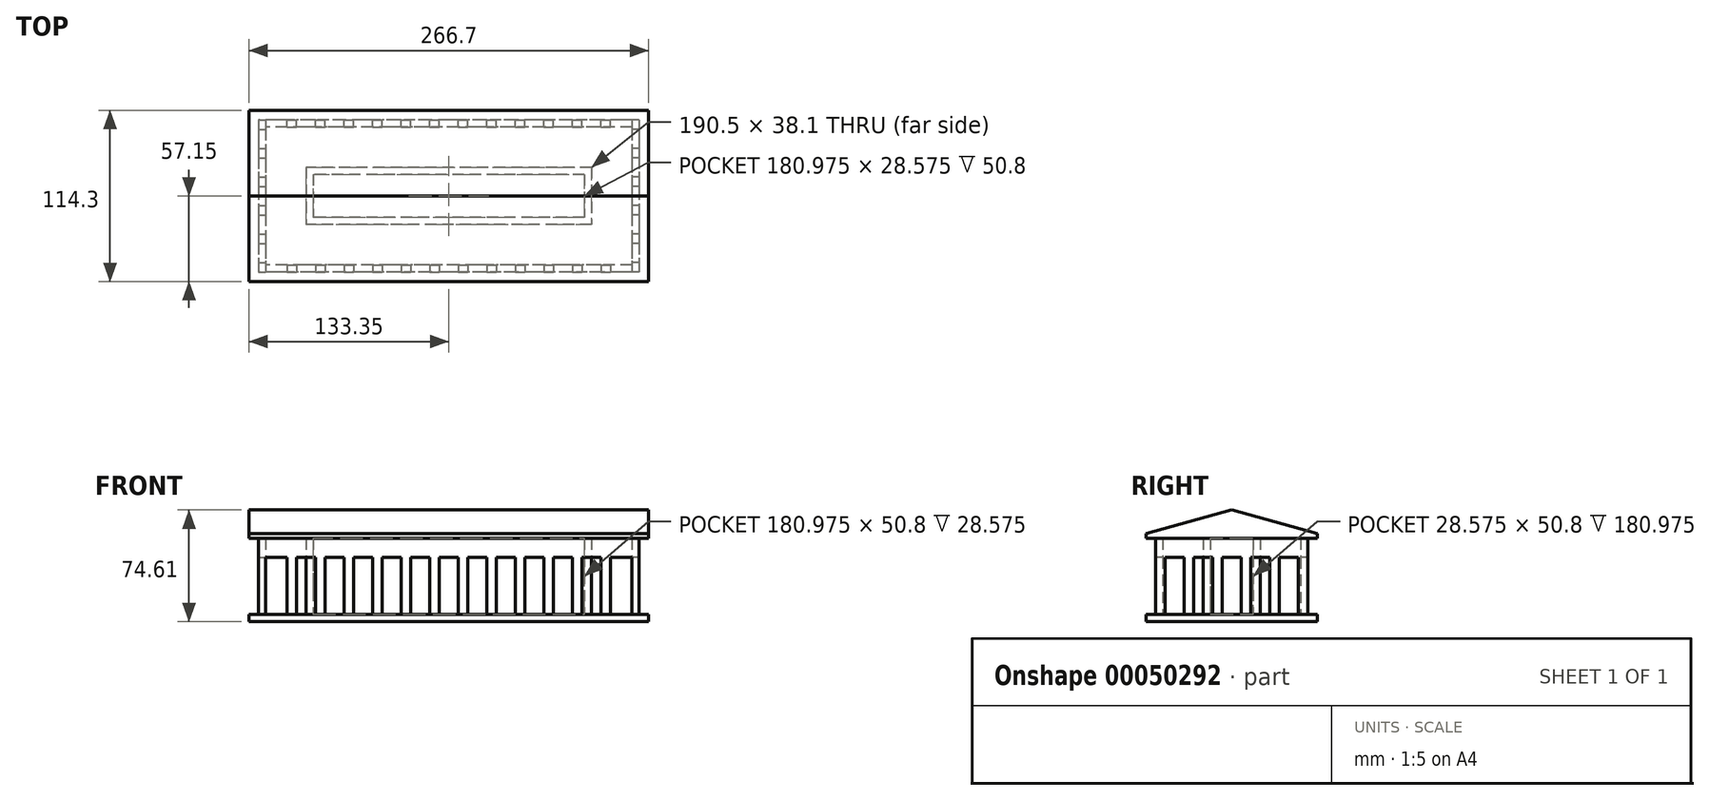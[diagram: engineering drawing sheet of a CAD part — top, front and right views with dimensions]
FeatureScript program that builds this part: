
annotation { "Feature Type Name" : "Feature", "Feature Type Description" : "" }
export const myFeature = defineFeature(function(context is Context, id is Id, definition is map)
    precondition{}
    {
        {
            var Q0;
            Q0=qCreatedBy(makeId("Top.planeOp"),FACE);
            var sketch = newSketch(context, id + "F0", { "sketchPlane" : qUnion([Q0])});
            skLineSegment(sketch, "E0.bottom", {"start": v(0, 0) * mm, "end": v(-266.7, 0) * mm});
            skLineSegment(sketch, "E0.top", {"start": v(0, -114.3) * mm, "end": v(-266.7, -114.3) * mm});
            skLineSegment(sketch, "E0.left", {"start": v(0, 0) * mm, "end": v(0, -114.3) * mm});
            skLineSegment(sketch, "E0.right", {"start": v(-266.7, 0) * mm, "end": v(-266.7, -114.3) * mm});
            skSolve(sketch);
        }
        {
            var Q0;
            Q0=qSketchRegion(id+"F0",true);
            var Q1;
            Q1=qSketchRegion(id+"FEWzJ1hWetXT4Pq_1",true);
            extrude(context, id + "F1", {"entities" : qUnion([Q0, Q1]), "depth" : 4.78 * mm});
        }
        {
            var Q0;
            Q0=makeQuery(id+"F1.opExtrude","CAP_FACE",FACE,{"disambiguationData":[OSD([sQuery(id+"F0.wireOp",EDGE,"E0.bottom"),sQuery(id+"F0.wireOp",EDGE,"E0.top"),sQuery(id+"F0.wireOp",EDGE,"E0.left"),sQuery(id+"F0.wireOp",EDGE,"E0.right")])],"isStart":false});
            var sketch = newSketch(context, id + "F2", { "sketchPlane" : qUnion([Q0])});
            skLineSegment(sketch, "E1.bottom", {"start": v(-260.35, -101.6) * mm, "end": v(-255.59, -101.6) * mm});
            skLineSegment(sketch, "E1.top", {"start": v(-260.35, -107.95) * mm, "end": v(-255.59, -107.95) * mm});
            skLineSegment(sketch, "E1.left", {"start": v(-260.35, -101.6) * mm, "end": v(-260.35, -107.95) * mm});
            skLineSegment(sketch, "E1.right", {"start": v(-255.59, -101.6) * mm, "end": v(-255.59, -107.95) * mm});
            skLineSegment(sketch, "E2.0.1.0", {"start": v(-260.35, -88.9) * mm, "end": v(-255.59, -88.9) * mm});
            skLineSegment(sketch, "E2.0.1.1", {"start": v(-255.59, -82.55) * mm, "end": v(-255.59, -88.9) * mm});
            skLineSegment(sketch, "E2.0.1.2", {"start": v(-260.35, -82.55) * mm, "end": v(-260.35, -88.9) * mm});
            skLineSegment(sketch, "E2.0.1.3", {"start": v(-260.35, -82.55) * mm, "end": v(-255.59, -82.55) * mm});
            skLineSegment(sketch, "E2.0.2.0", {"start": v(-260.35, -69.85) * mm, "end": v(-255.59, -69.85) * mm});
            skLineSegment(sketch, "E2.0.2.1", {"start": v(-255.59, -63.5) * mm, "end": v(-255.59, -69.85) * mm});
            skLineSegment(sketch, "E2.0.2.2", {"start": v(-260.35, -63.5) * mm, "end": v(-260.35, -69.85) * mm});
            skLineSegment(sketch, "E2.0.2.3", {"start": v(-260.35, -63.5) * mm, "end": v(-255.59, -63.5) * mm});
            skLineSegment(sketch, "E2.0.3.0", {"start": v(-260.35, -50.8) * mm, "end": v(-255.59, -50.8) * mm});
            skLineSegment(sketch, "E2.0.3.1", {"start": v(-255.59, -44.45) * mm, "end": v(-255.59, -50.8) * mm});
            skLineSegment(sketch, "E2.0.3.2", {"start": v(-260.35, -44.45) * mm, "end": v(-260.35, -50.8) * mm});
            skLineSegment(sketch, "E2.0.3.3", {"start": v(-260.35, -44.45) * mm, "end": v(-255.59, -44.45) * mm});
            skLineSegment(sketch, "E2.0.4.0", {"start": v(-260.35, -31.75) * mm, "end": v(-255.59, -31.75) * mm});
            skLineSegment(sketch, "E2.0.4.1", {"start": v(-255.59, -25.4) * mm, "end": v(-255.59, -31.75) * mm});
            skLineSegment(sketch, "E2.0.4.2", {"start": v(-260.35, -25.4) * mm, "end": v(-260.35, -31.75) * mm});
            skLineSegment(sketch, "E2.0.4.3", {"start": v(-260.35, -25.4) * mm, "end": v(-255.59, -25.4) * mm});
            skLineSegment(sketch, "E2.0.5.0", {"start": v(-260.35, -12.7) * mm, "end": v(-255.59, -12.7) * mm});
            skLineSegment(sketch, "E2.0.5.1", {"start": v(-255.59, -6.35) * mm, "end": v(-255.59, -12.7) * mm});
            skLineSegment(sketch, "E2.0.5.2", {"start": v(-260.35, -6.35) * mm, "end": v(-260.35, -12.7) * mm});
            skLineSegment(sketch, "E2.0.5.3", {"start": v(-260.35, -6.35) * mm, "end": v(-255.59, -6.35) * mm});
            skLineSegment(sketch, "E2.direction1", {"start": v(-260.35, -107.95) * mm, "end": v(-251.94, -107.95) * mm, "construction": true});
            skLineSegment(sketch, "E2.direction2", {"start": v(-260.35, -107.95) * mm, "end": v(-260.35, -88.9) * mm, "construction": true});
            skLineSegment(sketch, "E3.bottom", {"start": v(-241.3, -103.19) * mm, "end": v(-234.95, -103.19) * mm});
            skLineSegment(sketch, "E3.top", {"start": v(-241.3, -107.95) * mm, "end": v(-234.95, -107.95) * mm});
            skLineSegment(sketch, "E3.left", {"start": v(-241.3, -103.19) * mm, "end": v(-241.3, -107.95) * mm});
            skLineSegment(sketch, "E3.right", {"start": v(-234.95, -103.19) * mm, "end": v(-234.95, -107.95) * mm});
            skLineSegment(sketch, "E4.1.0.0", {"start": v(-222.25, -107.95) * mm, "end": v(-215.9, -107.95) * mm});
            skLineSegment(sketch, "E4.1.0.1", {"start": v(-215.9, -103.19) * mm, "end": v(-215.9, -107.95) * mm});
            skLineSegment(sketch, "E4.1.0.2", {"start": v(-222.25, -103.19) * mm, "end": v(-222.25, -107.95) * mm});
            skLineSegment(sketch, "E4.1.0.3", {"start": v(-222.25, -103.19) * mm, "end": v(-215.9, -103.19) * mm});
            skLineSegment(sketch, "E4.2.0.0", {"start": v(-203.2, -107.95) * mm, "end": v(-196.85, -107.95) * mm});
            skLineSegment(sketch, "E4.2.0.1", {"start": v(-196.85, -103.19) * mm, "end": v(-196.85, -107.95) * mm});
            skLineSegment(sketch, "E4.2.0.2", {"start": v(-203.2, -103.19) * mm, "end": v(-203.2, -107.95) * mm});
            skLineSegment(sketch, "E4.2.0.3", {"start": v(-203.2, -103.19) * mm, "end": v(-196.85, -103.19) * mm});
            skLineSegment(sketch, "E4.3.0.0", {"start": v(-184.15, -107.95) * mm, "end": v(-177.8, -107.95) * mm});
            skLineSegment(sketch, "E4.3.0.1", {"start": v(-177.8, -103.19) * mm, "end": v(-177.8, -107.95) * mm});
            skLineSegment(sketch, "E4.3.0.2", {"start": v(-184.15, -103.19) * mm, "end": v(-184.15, -107.95) * mm});
            skLineSegment(sketch, "E4.3.0.3", {"start": v(-184.15, -103.19) * mm, "end": v(-177.8, -103.19) * mm});
            skLineSegment(sketch, "E4.4.0.0", {"start": v(-165.1, -107.95) * mm, "end": v(-158.75, -107.95) * mm});
            skLineSegment(sketch, "E4.4.0.1", {"start": v(-158.75, -103.19) * mm, "end": v(-158.75, -107.95) * mm});
            skLineSegment(sketch, "E4.4.0.2", {"start": v(-165.1, -103.19) * mm, "end": v(-165.1, -107.95) * mm});
            skLineSegment(sketch, "E4.4.0.3", {"start": v(-165.1, -103.19) * mm, "end": v(-158.75, -103.19) * mm});
            skLineSegment(sketch, "E4.5.0.0", {"start": v(-146.05, -107.95) * mm, "end": v(-139.7, -107.95) * mm});
            skLineSegment(sketch, "E4.5.0.1", {"start": v(-139.7, -103.19) * mm, "end": v(-139.7, -107.95) * mm});
            skLineSegment(sketch, "E4.5.0.2", {"start": v(-146.05, -103.19) * mm, "end": v(-146.05, -107.95) * mm});
            skLineSegment(sketch, "E4.5.0.3", {"start": v(-146.05, -103.19) * mm, "end": v(-139.7, -103.19) * mm});
            skLineSegment(sketch, "E4.6.0.0", {"start": v(-127, -107.95) * mm, "end": v(-120.65, -107.95) * mm});
            skLineSegment(sketch, "E4.6.0.1", {"start": v(-120.65, -103.19) * mm, "end": v(-120.65, -107.95) * mm});
            skLineSegment(sketch, "E4.6.0.2", {"start": v(-127, -103.19) * mm, "end": v(-127, -107.95) * mm});
            skLineSegment(sketch, "E4.6.0.3", {"start": v(-127, -103.19) * mm, "end": v(-120.65, -103.19) * mm});
            skLineSegment(sketch, "E4.7.0.0", {"start": v(-107.95, -107.95) * mm, "end": v(-101.6, -107.95) * mm});
            skLineSegment(sketch, "E4.7.0.1", {"start": v(-101.6, -103.19) * mm, "end": v(-101.6, -107.95) * mm});
            skLineSegment(sketch, "E4.7.0.2", {"start": v(-107.95, -103.19) * mm, "end": v(-107.95, -107.95) * mm});
            skLineSegment(sketch, "E4.7.0.3", {"start": v(-107.95, -103.19) * mm, "end": v(-101.6, -103.19) * mm});
            skLineSegment(sketch, "E4.8.0.0", {"start": v(-88.9, -107.95) * mm, "end": v(-82.55, -107.95) * mm});
            skLineSegment(sketch, "E4.8.0.1", {"start": v(-82.55, -103.19) * mm, "end": v(-82.55, -107.95) * mm});
            skLineSegment(sketch, "E4.8.0.2", {"start": v(-88.9, -103.19) * mm, "end": v(-88.9, -107.95) * mm});
            skLineSegment(sketch, "E4.8.0.3", {"start": v(-88.9, -103.19) * mm, "end": v(-82.55, -103.19) * mm});
            skLineSegment(sketch, "E4.9.0.0", {"start": v(-69.85, -107.95) * mm, "end": v(-63.5, -107.95) * mm});
            skLineSegment(sketch, "E4.9.0.1", {"start": v(-63.5, -103.19) * mm, "end": v(-63.5, -107.95) * mm});
            skLineSegment(sketch, "E4.9.0.2", {"start": v(-69.85, -103.19) * mm, "end": v(-69.85, -107.95) * mm});
            skLineSegment(sketch, "E4.9.0.3", {"start": v(-69.85, -103.19) * mm, "end": v(-63.5, -103.19) * mm});
            skLineSegment(sketch, "E4.10.0.0", {"start": v(-50.8, -107.95) * mm, "end": v(-44.45, -107.95) * mm});
            skLineSegment(sketch, "E4.10.0.1", {"start": v(-44.45, -103.19) * mm, "end": v(-44.45, -107.95) * mm});
            skLineSegment(sketch, "E4.10.0.2", {"start": v(-50.8, -103.19) * mm, "end": v(-50.8, -107.95) * mm});
            skLineSegment(sketch, "E4.10.0.3", {"start": v(-50.8, -103.19) * mm, "end": v(-44.45, -103.19) * mm});
            skLineSegment(sketch, "E4.11.0.0", {"start": v(-31.75, -107.95) * mm, "end": v(-25.4, -107.95) * mm});
            skLineSegment(sketch, "E4.11.0.1", {"start": v(-25.4, -103.19) * mm, "end": v(-25.4, -107.95) * mm});
            skLineSegment(sketch, "E4.11.0.2", {"start": v(-31.75, -103.19) * mm, "end": v(-31.75, -107.95) * mm});
            skLineSegment(sketch, "E4.11.0.3", {"start": v(-31.75, -103.19) * mm, "end": v(-25.4, -103.19) * mm});
            skLineSegment(sketch, "E4.direction1", {"start": v(-241.3, -107.95) * mm, "end": v(-222.25, -107.95) * mm, "construction": true});
            skLineSegment(sketch, "E5.MirrorCS", {"start": v(-6.35, -107.95) * mm, "end": v(-11.11, -107.95) * mm});
            skLineSegment(sketch, "E6.MirrorCS", {"start": v(-6.35, -82.55) * mm, "end": v(-6.35, -88.9) * mm});
            skLineSegment(sketch, "E7.MirrorCS", {"start": v(-6.35, -82.55) * mm, "end": v(-11.11, -82.55) * mm});
            skLineSegment(sketch, "E8.MirrorCS", {"start": v(-6.35, -12.7) * mm, "end": v(-11.11, -12.7) * mm});
            skLineSegment(sketch, "E9.MirrorCS", {"start": v(-11.11, -6.35) * mm, "end": v(-11.11, -12.7) * mm});
            skLineSegment(sketch, "E10.MirrorCS", {"start": v(-6.35, -6.35) * mm, "end": v(-6.35, -12.7) * mm});
            skLineSegment(sketch, "E11.MirrorCS", {"start": v(-6.35, -6.35) * mm, "end": v(-11.11, -6.35) * mm});
            skLineSegment(sketch, "E12.MirrorCS", {"start": v(-6.35, -31.75) * mm, "end": v(-11.11, -31.75) * mm});
            skLineSegment(sketch, "E13.MirrorCS", {"start": v(-11.11, -25.4) * mm, "end": v(-11.11, -31.75) * mm});
            skLineSegment(sketch, "E14.MirrorCS", {"start": v(-11.11, -44.45) * mm, "end": v(-11.11, -50.8) * mm});
            skLineSegment(sketch, "E15.MirrorCS", {"start": v(-6.35, -44.45) * mm, "end": v(-6.35, -50.8) * mm});
            skLineSegment(sketch, "E16.MirrorCS", {"start": v(-6.35, -44.45) * mm, "end": v(-11.11, -44.45) * mm});
            skLineSegment(sketch, "E17.MirrorCS", {"start": v(-6.35, -25.4) * mm, "end": v(-6.35, -31.75) * mm});
            skLineSegment(sketch, "E18.MirrorCS", {"start": v(-11.11, -63.5) * mm, "end": v(-11.11, -69.85) * mm});
            skLineSegment(sketch, "E19.MirrorCS", {"start": v(-6.35, -101.6) * mm, "end": v(-11.11, -101.6) * mm});
            skLineSegment(sketch, "E20.MirrorCS", {"start": v(-6.35, -101.6) * mm, "end": v(-6.35, -107.95) * mm});
            skLineSegment(sketch, "E21.MirrorCS", {"start": v(-6.35, -63.5) * mm, "end": v(-6.35, -69.85) * mm});
            skLineSegment(sketch, "E22.MirrorCS", {"start": v(-6.35, -69.85) * mm, "end": v(-11.11, -69.85) * mm});
            skLineSegment(sketch, "E23.MirrorCS", {"start": v(-11.11, -101.6) * mm, "end": v(-11.11, -107.95) * mm});
            skLineSegment(sketch, "E24.MirrorCS", {"start": v(-6.35, -88.9) * mm, "end": v(-11.11, -88.9) * mm});
            skLineSegment(sketch, "E25.MirrorCS", {"start": v(-6.35, -63.5) * mm, "end": v(-11.11, -63.5) * mm});
            skLineSegment(sketch, "E26.MirrorCS", {"start": v(-6.35, -50.8) * mm, "end": v(-11.11, -50.8) * mm});
            skLineSegment(sketch, "E27.MirrorCS", {"start": v(-11.11, -82.55) * mm, "end": v(-11.11, -88.9) * mm});
            skLineSegment(sketch, "E28.MirrorCS", {"start": v(-6.35, -25.4) * mm, "end": v(-11.11, -25.4) * mm});
            skLineSegment(sketch, "E29.direction1", {"start": v(0, 0) * mm, "end": v(25.4, 0) * mm, "construction": true});
            skLineSegment(sketch, "E30.MirrorCS", {"start": v(-120.65, -11.11) * mm, "end": v(-120.65, -6.35) * mm});
            skLineSegment(sketch, "E31.MirrorCS", {"start": v(-203.2, -6.35) * mm, "end": v(-196.85, -6.35) * mm});
            skLineSegment(sketch, "E32.MirrorCS", {"start": v(-184.15, -11.11) * mm, "end": v(-177.8, -11.11) * mm});
            skLineSegment(sketch, "E33.MirrorCS", {"start": v(-31.75, -11.11) * mm, "end": v(-25.4, -11.11) * mm});
            skLineSegment(sketch, "E34.MirrorCS", {"start": v(-203.2, -11.11) * mm, "end": v(-203.2, -6.35) * mm});
            skLineSegment(sketch, "E35.MirrorCS", {"start": v(-177.8, -11.11) * mm, "end": v(-177.8, -6.35) * mm});
            skLineSegment(sketch, "E36.MirrorCS", {"start": v(-196.85, -11.11) * mm, "end": v(-196.85, -6.35) * mm});
            skLineSegment(sketch, "E37.MirrorCS", {"start": v(-165.1, -6.35) * mm, "end": v(-158.75, -6.35) * mm});
            skLineSegment(sketch, "E38.MirrorCS", {"start": v(-25.4, -11.11) * mm, "end": v(-25.4, -6.35) * mm});
            skLineSegment(sketch, "E39.MirrorCS", {"start": v(-241.3, -11.11) * mm, "end": v(-234.95, -11.11) * mm});
            skLineSegment(sketch, "E40.MirrorCS", {"start": v(-88.9, -6.35) * mm, "end": v(-82.55, -6.35) * mm});
            skLineSegment(sketch, "E41.MirrorCS", {"start": v(-165.1, -11.11) * mm, "end": v(-158.75, -11.11) * mm});
            skLineSegment(sketch, "E42.MirrorCS", {"start": v(-146.05, -11.11) * mm, "end": v(-146.05, -6.35) * mm});
            skLineSegment(sketch, "E43.MirrorCS", {"start": v(-69.85, -11.11) * mm, "end": v(-69.85, -6.35) * mm});
            skLineSegment(sketch, "E44.MirrorCS", {"start": v(-88.9, -11.11) * mm, "end": v(-88.9, -6.35) * mm});
            skLineSegment(sketch, "E45.MirrorCS", {"start": v(-234.95, -11.11) * mm, "end": v(-234.95, -6.35) * mm});
            skLineSegment(sketch, "E46.MirrorCS", {"start": v(-165.1, -11.11) * mm, "end": v(-165.1, -6.35) * mm});
            skLineSegment(sketch, "E47.MirrorCS", {"start": v(-241.3, -11.11) * mm, "end": v(-241.3, -6.35) * mm});
            skLineSegment(sketch, "E48.MirrorCS", {"start": v(-222.25, -6.35) * mm, "end": v(-215.9, -6.35) * mm});
            skLineSegment(sketch, "E49.MirrorCS", {"start": v(-203.2, -11.11) * mm, "end": v(-196.85, -11.11) * mm});
            skLineSegment(sketch, "E50.MirrorCS", {"start": v(-146.05, -11.11) * mm, "end": v(-139.7, -11.11) * mm});
            skLineSegment(sketch, "E51.MirrorCS", {"start": v(-107.95, -6.35) * mm, "end": v(-101.6, -6.35) * mm});
            skLineSegment(sketch, "E52.MirrorCS", {"start": v(-63.5, -11.11) * mm, "end": v(-63.5, -6.35) * mm});
            skLineSegment(sketch, "E53.MirrorCS", {"start": v(-127, -6.35) * mm, "end": v(-120.65, -6.35) * mm});
            skLineSegment(sketch, "E54.MirrorCS", {"start": v(-69.85, -11.11) * mm, "end": v(-63.5, -11.11) * mm});
            skLineSegment(sketch, "E55.MirrorCS", {"start": v(-50.8, -6.35) * mm, "end": v(-44.45, -6.35) * mm});
            skLineSegment(sketch, "E56.MirrorCS", {"start": v(-184.15, -11.11) * mm, "end": v(-184.15, -6.35) * mm});
            skLineSegment(sketch, "E57.MirrorCS", {"start": v(-107.95, -11.11) * mm, "end": v(-101.6, -11.11) * mm});
            skLineSegment(sketch, "E58.MirrorCS", {"start": v(-241.3, -6.35) * mm, "end": v(-234.95, -6.35) * mm});
            skLineSegment(sketch, "E59.MirrorCS", {"start": v(-50.8, -11.11) * mm, "end": v(-50.8, -6.35) * mm});
            skLineSegment(sketch, "E60.MirrorCS", {"start": v(-107.95, -11.11) * mm, "end": v(-107.95, -6.35) * mm});
            skLineSegment(sketch, "E61.MirrorCS", {"start": v(-44.45, -11.11) * mm, "end": v(-44.45, -6.35) * mm});
            skLineSegment(sketch, "E62.MirrorCS", {"start": v(-222.25, -11.11) * mm, "end": v(-222.25, -6.35) * mm});
            skLineSegment(sketch, "E63.MirrorCS", {"start": v(-82.55, -11.11) * mm, "end": v(-82.55, -6.35) * mm});
            skLineSegment(sketch, "E64.MirrorCS", {"start": v(-101.6, -11.11) * mm, "end": v(-101.6, -6.35) * mm});
            skLineSegment(sketch, "E65.MirrorCS", {"start": v(-31.75, -11.11) * mm, "end": v(-31.75, -6.35) * mm});
            skLineSegment(sketch, "E66.MirrorCS", {"start": v(-88.9, -11.11) * mm, "end": v(-82.55, -11.11) * mm});
            skLineSegment(sketch, "E67.MirrorCS", {"start": v(-139.7, -11.11) * mm, "end": v(-139.7, -6.35) * mm});
            skLineSegment(sketch, "E68.MirrorCS", {"start": v(-31.75, -6.35) * mm, "end": v(-25.4, -6.35) * mm});
            skLineSegment(sketch, "E69.MirrorCS", {"start": v(-50.8, -11.11) * mm, "end": v(-44.45, -11.11) * mm});
            skLineSegment(sketch, "E70.MirrorCS", {"start": v(-69.85, -6.35) * mm, "end": v(-63.5, -6.35) * mm});
            skLineSegment(sketch, "E71.MirrorCS", {"start": v(-127, -11.11) * mm, "end": v(-120.65, -11.11) * mm});
            skLineSegment(sketch, "E72.MirrorCS", {"start": v(-127, -11.11) * mm, "end": v(-127, -6.35) * mm});
            skLineSegment(sketch, "E73.MirrorCS", {"start": v(-222.25, -11.11) * mm, "end": v(-215.9, -11.11) * mm});
            skLineSegment(sketch, "E74.MirrorCS", {"start": v(-215.9, -11.11) * mm, "end": v(-215.9, -6.35) * mm});
            skLineSegment(sketch, "E75.MirrorCS", {"start": v(-146.05, -6.35) * mm, "end": v(-139.7, -6.35) * mm});
            skLineSegment(sketch, "E76.MirrorCS", {"start": v(-158.75, -11.11) * mm, "end": v(-158.75, -6.35) * mm});
            skLineSegment(sketch, "E77.MirrorCS", {"start": v(-184.15, -6.35) * mm, "end": v(-177.8, -6.35) * mm});
            skSolve(sketch);
        }
        {
            var Q0;
            Q0=qSketchRegion(id+"F2",true);
            var Q1;
            Q1=qSketchRegion(id+"F6IGndgWyHRMqrs_1",true);
            extrude(context, id + "F3", {"entities" : qUnion([Q0, Q1]), "operationType" : NewBodyOperationType.ADD, "depth" : 38.1 * mm});
        }
        {
            var Q0;
            Q0=makeQuery(id+"F1.opExtrude","CAP_FACE",FACE,{"disambiguationData":[OSD([sQuery(id+"F0.wireOp",EDGE,"E0.bottom"),sQuery(id+"F0.wireOp",EDGE,"E0.top"),sQuery(id+"F0.wireOp",EDGE,"E0.left"),sQuery(id+"F0.wireOp",EDGE,"E0.right")])],"isStart":false});
            var sketch = newSketch(context, id + "F4", { "sketchPlane" : qUnion([Q0])});
            skLineSegment(sketch, "E78.0", {"start": v(-38.1, -38.1) * mm, "end": v(-228.6, -38.1) * mm});
            skLineSegment(sketch, "E78.1", {"start": v(-38.1, -38.1) * mm, "end": v(-38.1, -76.2) * mm});
            skLineSegment(sketch, "E78.2", {"start": v(-38.1, -76.2) * mm, "end": v(-228.6, -76.2) * mm});
            skLineSegment(sketch, "E78.3", {"start": v(-228.6, -38.1) * mm, "end": v(-228.6, -76.2) * mm});
            skLineSegment(sketch, "E79.0", {"start": v(-42.86, -42.86) * mm, "end": v(-223.84, -42.86) * mm});
            skLineSegment(sketch, "E79.1", {"start": v(-42.86, -42.86) * mm, "end": v(-42.86, -71.44) * mm});
            skLineSegment(sketch, "E79.2", {"start": v(-42.86, -71.44) * mm, "end": v(-223.84, -71.44) * mm});
            skLineSegment(sketch, "E79.3", {"start": v(-223.84, -42.86) * mm, "end": v(-223.84, -71.44) * mm});
            skLineSegment(sketch, "E80.0", {"start": v(-6.35, -107.95) * mm, "end": v(-6.35, -6.35) * mm});
            skLineSegment(sketch, "E80.1", {"start": v(-260.35, -107.95) * mm, "end": v(-6.35, -107.95) * mm});
            skLineSegment(sketch, "E80.2", {"start": v(-260.35, -6.35) * mm, "end": v(-260.35, -107.95) * mm});
            skLineSegment(sketch, "E80.3", {"start": v(-6.35, -6.35) * mm, "end": v(-260.35, -6.35) * mm});
            skLineSegment(sketch, "E81.0", {"start": v(0, -107.95) * mm, "end": v(0, -6.35) * mm});
            skSolve(sketch);
        }
        {
            var Q0;
            Q0=makeQuery(id+"F4.imprint","IMPRINT",FACE,{"disambiguationData":[TD([[makeQuery(id+"F4.imprint","IMPRINT",EDGE,{"derivedFrom":sQuery(id+"F4.wireOp",EDGE,"E78.0")}),1.0]])]});
            extrude(context, id + "F5", {"entities" : qUnion([Q0]), "operationType" : NewBodyOperationType.ADD, "depth" : 50.8 * mm});
        }
        {
            var Q0;
            Q0=makeQuery(id+"F3.opExtrude","CAP_FACE",FACE,{"disambiguationData":[OSD([sQuery(id+"F2.wireOp",EDGE,"E48.MirrorCS"),sQuery(id+"F2.wireOp",EDGE,"E62.MirrorCS"),sQuery(id+"F2.wireOp",EDGE,"E73.MirrorCS"),sQuery(id+"F2.wireOp",EDGE,"E74.MirrorCS")])],"isStart":false});
            var sketch = newSketch(context, id + "F6", { "sketchPlane" : qUnion([Q0])});
            skLineSegment(sketch, "E82.bottom", {"start": v(-6.35, -6.35) * mm, "end": v(-260.35, -6.35) * mm});
            skLineSegment(sketch, "E82.top", {"start": v(-6.35, -107.95) * mm, "end": v(-260.35, -107.95) * mm});
            skLineSegment(sketch, "E82.left", {"start": v(-6.35, -6.35) * mm, "end": v(-6.35, -107.95) * mm});
            skLineSegment(sketch, "E82.right", {"start": v(-260.35, -6.35) * mm, "end": v(-260.35, -107.95) * mm});
            skLineSegment(sketch, "E83.0", {"start": v(-11.11, -11.11) * mm, "end": v(-255.59, -11.11) * mm});
            skLineSegment(sketch, "E83.1", {"start": v(-11.11, -11.11) * mm, "end": v(-11.11, -103.19) * mm});
            skLineSegment(sketch, "E83.2", {"start": v(-11.11, -103.19) * mm, "end": v(-255.59, -103.19) * mm});
            skLineSegment(sketch, "E83.3", {"start": v(-255.59, -11.11) * mm, "end": v(-255.59, -103.19) * mm});
            skLineSegment(sketch, "E84.0", {"start": v(-6.35, -107.95) * mm, "end": v(-6.35, -6.35) * mm});
            skLineSegment(sketch, "E84.1", {"start": v(-260.35, -107.95) * mm, "end": v(-6.35, -107.95) * mm});
            skSolve(sketch);
        }
        {
            var Q0;
            Q0=qSketchRegion(id+"F6",true);
            extrude(context, id + "F7", {"entities" : qUnion([Q0]), "operationType" : NewBodyOperationType.ADD, "depth" : 12.7 * mm});
        }
        {
            var Q0;
            Q0=makeQuery(id+"F1.opExtrude","SWEPT_FACE",FACE,{"disambiguationData":[OSD([sQuery(id+"F0.wireOp",EDGE,"E0.right")])]});
            var sketch = newSketch(context, id + "F8", { "sketchPlane" : qUnion([Q0])});
            skLineSegment(sketch, "E85.0.0", {"start": v(101.6, 4.78) * mm, "end": v(107.95, 4.78) * mm});
            skLineSegment(sketch, "E85.0.1", {"start": v(107.95, 4.78) * mm, "end": v(107.95, 55.58) * mm});
            skLineSegment(sketch, "E85.0.2", {"start": v(107.95, 55.58) * mm, "end": v(6.35, 55.58) * mm});
            skLineSegment(sketch, "E85.0.3", {"start": v(6.35, 55.58) * mm, "end": v(6.35, 4.78) * mm});
            skLineSegment(sketch, "E85.0.4", {"start": v(6.35, 4.78) * mm, "end": v(12.7, 4.78) * mm});
            skLineSegment(sketch, "E85.0.5", {"start": v(12.7, 4.78) * mm, "end": v(12.7, 42.88) * mm});
            skLineSegment(sketch, "E85.0.6", {"start": v(12.7, 42.88) * mm, "end": v(25.4, 42.88) * mm});
            skLineSegment(sketch, "E85.0.7", {"start": v(25.4, 42.88) * mm, "end": v(25.4, 4.78) * mm});
            skLineSegment(sketch, "E85.0.8", {"start": v(25.4, 4.78) * mm, "end": v(31.75, 4.78) * mm});
            skLineSegment(sketch, "E85.0.9", {"start": v(31.75, 4.78) * mm, "end": v(31.75, 42.88) * mm});
            skLineSegment(sketch, "E85.0.10", {"start": v(31.75, 42.88) * mm, "end": v(44.45, 42.88) * mm});
            skLineSegment(sketch, "E85.0.11", {"start": v(44.45, 42.88) * mm, "end": v(44.45, 4.78) * mm});
            skLineSegment(sketch, "E85.0.12", {"start": v(44.45, 4.78) * mm, "end": v(50.8, 4.78) * mm});
            skLineSegment(sketch, "E85.0.13", {"start": v(50.8, 4.78) * mm, "end": v(50.8, 42.88) * mm});
            skLineSegment(sketch, "E85.0.14", {"start": v(50.8, 42.88) * mm, "end": v(63.5, 42.88) * mm});
            skLineSegment(sketch, "E85.0.15", {"start": v(63.5, 42.88) * mm, "end": v(63.5, 4.78) * mm});
            skLineSegment(sketch, "E85.0.16", {"start": v(63.5, 4.78) * mm, "end": v(69.85, 4.78) * mm});
            skLineSegment(sketch, "E85.0.17", {"start": v(69.85, 4.78) * mm, "end": v(69.85, 42.88) * mm});
            skLineSegment(sketch, "E85.0.18", {"start": v(69.85, 42.88) * mm, "end": v(82.55, 42.88) * mm});
            skLineSegment(sketch, "E85.0.19", {"start": v(82.55, 42.88) * mm, "end": v(82.55, 4.78) * mm});
            skLineSegment(sketch, "E85.0.20", {"start": v(82.55, 4.78) * mm, "end": v(88.9, 4.78) * mm});
            skLineSegment(sketch, "E85.0.21", {"start": v(88.9, 4.78) * mm, "end": v(88.9, 42.88) * mm});
            skLineSegment(sketch, "E85.0.22", {"start": v(88.9, 42.88) * mm, "end": v(101.6, 42.88) * mm});
            skLineSegment(sketch, "E85.0.23", {"start": v(101.6, 42.88) * mm, "end": v(101.6, 4.78) * mm});
            skLineSegment(sketch, "E86", {"start": v(0, 55.58) * mm, "end": v(6.35, 55.58) * mm});
            skLineSegment(sketch, "E87", {"start": v(107.95, 55.58) * mm, "end": v(114.3, 55.58) * mm});
            skLineSegment(sketch, "E88", {"start": v(0, 55.58) * mm, "end": v(0, 58.75) * mm});
            skLineSegment(sketch, "E89", {"start": v(0, 58.75) * mm, "end": v(114.3, 58.75) * mm});
            skLineSegment(sketch, "E90", {"start": v(114.3, 58.75) * mm, "end": v(114.3, 55.58) * mm});
            skLineSegment(sketch, "E91", {"start": v(0, 58.75) * mm, "end": v(57.15, 74.61) * mm});
            skLineSegment(sketch, "E92", {"start": v(57.15, 74.61) * mm, "end": v(114.3, 58.75) * mm});
            skSolve(sketch);
        }
        {
            var Q0;
            Q0=makeQuery(id+"F8.imprint","IMPRINT",FACE,{"disambiguationData":[TD([[makeQuery(id+"F8.imprint","IMPRINT",EDGE,{"derivedFrom":sQuery(id+"F8.wireOp",EDGE,"E89")}),1.0]])]});
            var Q1;
            Q1=makeQuery(id+"F8.imprint","IMPRINT",FACE,{"disambiguationData":[TD([[makeQuery(id+"F8.imprint","IMPRINT",EDGE,{"derivedFrom":sQuery(id+"F8.wireOp",EDGE,"E85.0.2")}),-1.0]])]});
            var Q2;
            Q2=makeQuery(id+"F1.opExtrude","SWEPT_FACE",FACE,{"disambiguationData":[OSD([sQuery(id+"F0.wireOp",EDGE,"E0.left")])]});
            extrude(context, id + "F9", {"entities" : qUnion([Q0, Q1]), "operationType" : NewBodyOperationType.ADD, "endBound" : BoundingType.UP_TO_SURFACE, "oppositeDirection" : true, "endBoundEntityFace" : qUnion([Q2]), "depth" : 25.4 * mm});
        }
    });
